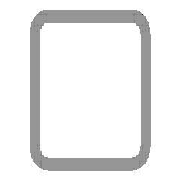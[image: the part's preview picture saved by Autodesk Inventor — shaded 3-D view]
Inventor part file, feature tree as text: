
AUTODESK INVENTOR PART (.ipt)
format: ipt  version: 2022 (Build 260153000, 153)  size: 147,456 bytes
history: native  units: mm (DEFAULTED — no unit token found)
features: other x4, sketch x3, plane x2, split x1
ambient origin geometry x8: Origin, YZ Plane, XZ Plane, XY Plane, X Axis, Y Axis, Z Axis, Center Point
bodies: Solid1 (feature_tree), Body (feature_tree)
feature tree (10):
  parser-record x1  (decoder bookkeeping rows leaked as tree rows — omitted from the tree; the rows remain in map.json)
  other  "Driven Length"
  other  "Start Plane"
  other  "End Plane"
  plane  "Work Plane4"
  split  "Split1"
  sketch  "Sketch"  dims[d7=8.0mm d9=40.0mm d11=40.0mm d12=4.0mm d13=-8.284271mm d14=110.0mm d15=20.0mm d16=20.0mm d17=90.0deg d18=118.284271mm]
  sketch  "Sketch3"  dims[d3=118.284271mm]
  plane  "Work Plane3"
  sketch  "Sketch4"  dims[d4=0.0mm]
